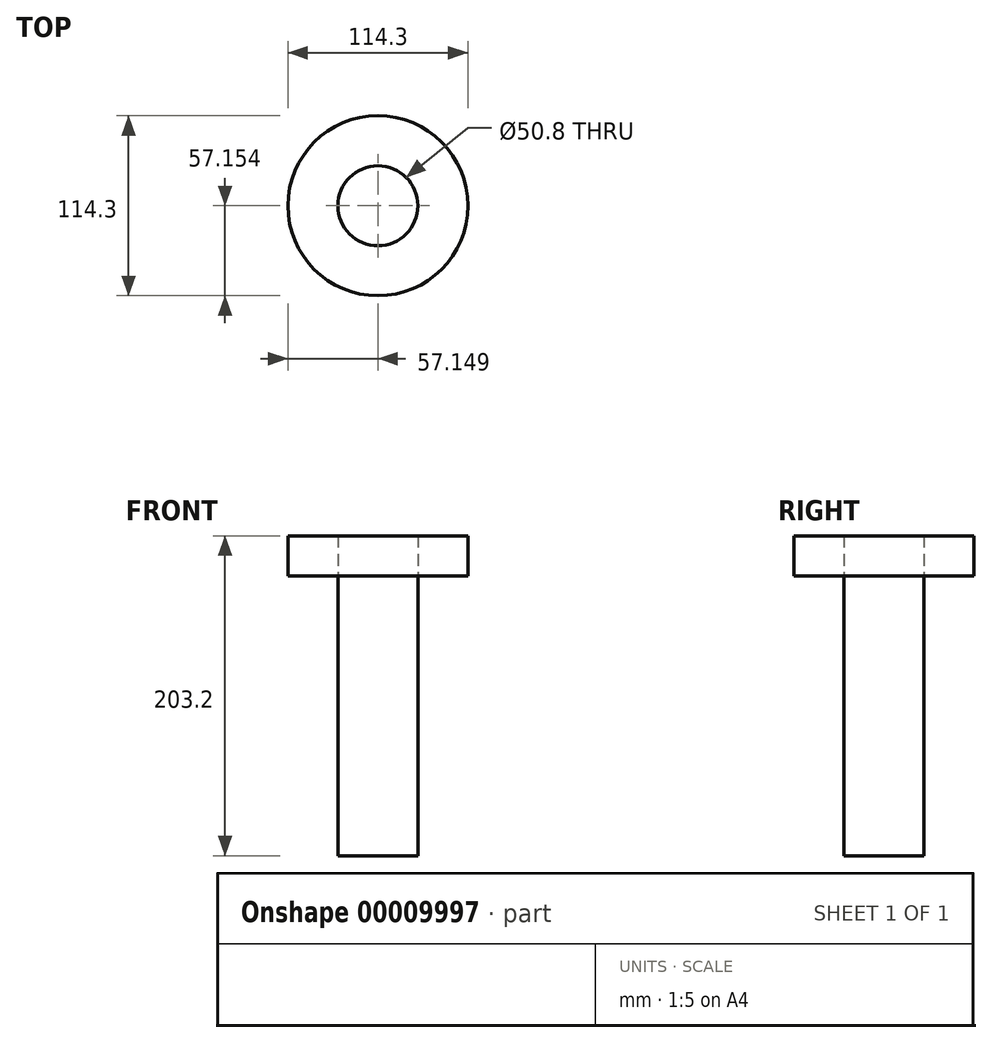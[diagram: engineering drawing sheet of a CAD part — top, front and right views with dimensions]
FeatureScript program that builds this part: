
annotation { "Feature Type Name" : "Feature", "Feature Type Description" : "" }
export const myFeature = defineFeature(function(context is Context, id is Id, definition is map)
    precondition{}
    {
        {
            var Q0;
            Q0=qCreatedBy(makeId("Top.planeOp"),FACE);
            var sketch = newSketch(context, id + "F0", { "sketchPlane" : qUnion([Q0])});
            skCircle(sketch, "E0", {"center": v(-31.18, 35.94) * mm, "radius": 25.4 * mm});
            skSolve(sketch);
        }
        {
            var Q0;
            Q0 = qSketchRegion(id + "F0", true);
            var Q1;
            Q1=makeQuery(id+"F0.imprint","IMPRINT",FACE,{"disambiguationData":[TD([[makeQuery(id+"F0.imprint","IMPRINT",EDGE,{"derivedFrom":sQuery(id+"F0.wireOp",EDGE,"E0")}),1.0]])]});
            extrude(context, id + "F1", {"entities" : qUnion([Q0, Q1]), "depth" : 177.8 * mm});
        }
        {
            var Q0;
            Q0=makeQuery(id+"F1.opExtrude","CAP_FACE",FACE,{"disambiguationData":[OSD([sQuery(id+"F0.wireOp",EDGE,"E0")])],"isStart":false});
            var sketch = newSketch(context, id + "F2", { "sketchPlane" : qUnion([Q0])});
            skCircle(sketch, "E1", {"center": v(-31.18, 35.94) * mm, "radius": 57.15 * mm});
            skSolve(sketch);
        }
        {
            var Q0;
            Q0=makeQuery(id+"F2.imprint","IMPRINT",FACE,{"disambiguationData":[TD([[makeQuery(id+"F2.imprint","IMPRINT",EDGE,{"derivedFrom":sQuery(id+"F2.wireOp",EDGE,"E1")}),1.0]])]});
            extrude(context, id + "F3", {"entities" : qUnion([Q0]), "depth" : 25.4 * mm});
        }
        {
            var Q0;
            Q0=makeQuery(id+"F1.opExtrude","CAP_FACE",FACE,{"disambiguationData":[OSD([sQuery(id+"F0.wireOp",EDGE,"E0")])],"isStart":false});
            extrude(context, id + "F4", {"entities" : qUnion([Q0]), "depth" : 25.4 * mm});
        }
    });
